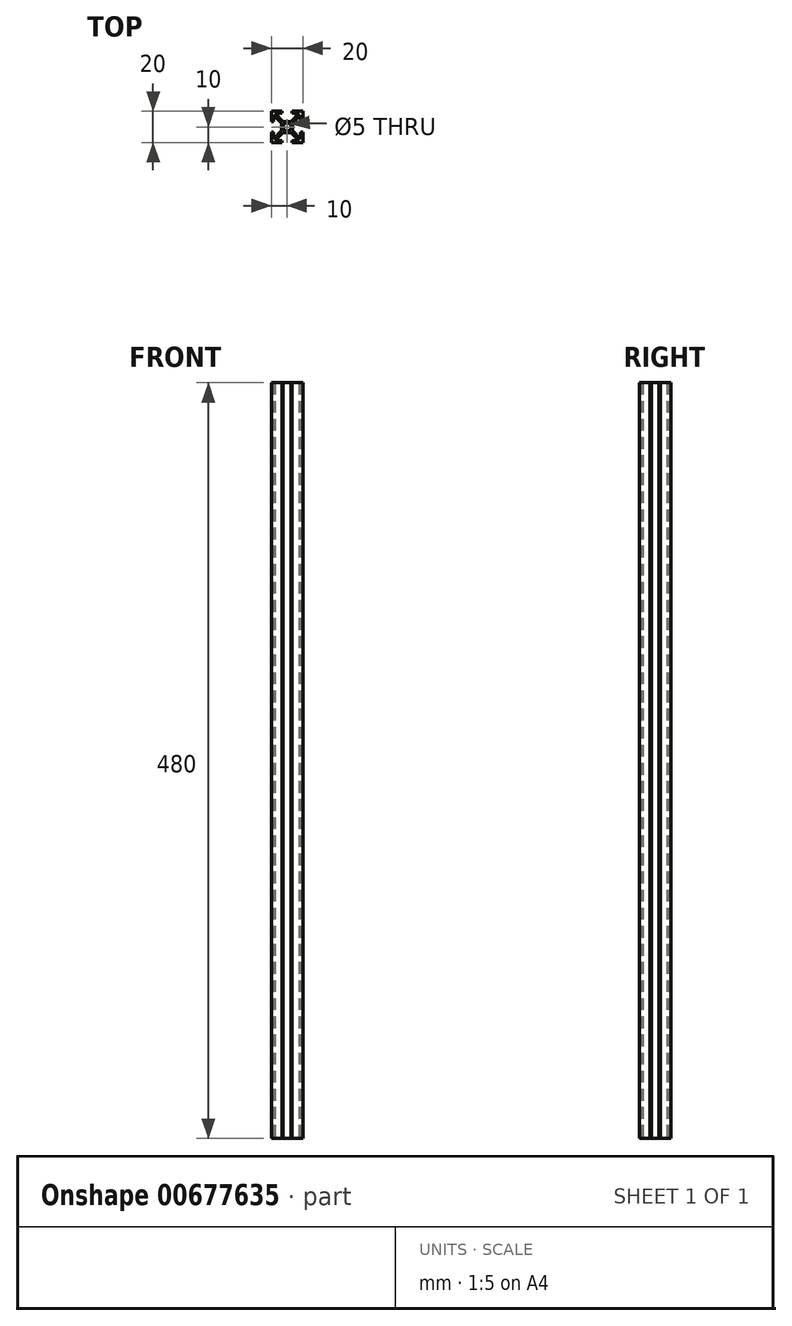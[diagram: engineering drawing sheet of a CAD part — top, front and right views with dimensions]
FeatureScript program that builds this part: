
annotation { "Feature Type Name" : "Feature", "Feature Type Description" : "" }
export const myFeature = defineFeature(function(context is Context, id is Id, definition is map)
    precondition{}
    {
        {
            var Q0;
            Q0=qCreatedBy(makeId("Top.planeOp"),FACE);
            var sketch = newSketch(context, id + "F0", { "sketchPlane" : qUnion([Q0])});
            skCircle(sketch, "E0", {"center": v(10, 10) * mm, "radius": 2.5 * mm});
            skLineSegment(sketch, "E1", {"start": v(0, 0) * mm, "end": v(10, 10) * mm, "construction": true});
            skLineSegment(sketch, "E2", {"start": v(1.4, 2.39) * mm, "end": v(1.4, 6.8) * mm});
            skLineSegment(sketch, "E3", {"start": v(1.4, 6.8) * mm, "end": v(0, 6.8) * mm});
            skLineSegment(sketch, "E4", {"start": v(0, 6.8) * mm, "end": v(0, 0) * mm});
            skLineSegment(sketch, "E5", {"start": v(7.49, 6.5) * mm, "end": v(2.39, 1.4) * mm});
            skLineSegment(sketch, "E6", {"start": v(2.39, 1.4) * mm, "end": v(6.8, 1.4) * mm});
            skLineSegment(sketch, "E7", {"start": v(6.8, 1.4) * mm, "end": v(6.8, 0) * mm});
            skLineSegment(sketch, "E8", {"start": v(6.8, 0) * mm, "end": v(0, 0) * mm});
            skLineSegment(sketch, "E9", {"start": v(10, 10) * mm, "end": v(20, 20) * mm, "construction": true});
            skLineSegment(sketch, "E10", {"start": v(10, 10) * mm, "end": v(0, 20) * mm, "construction": true});
            skLineSegment(sketch, "E11", {"start": v(10, 10) * mm, "end": v(20, 0) * mm, "construction": true});
            skLineSegment(sketch, "E12", {"start": v(1.4, 17.61) * mm, "end": v(6.5, 12.51) * mm});
            skLineSegment(sketch, "E13", {"start": v(1.4, 17.61) * mm, "end": v(1.4, 13.2) * mm});
            skLineSegment(sketch, "E14", {"start": v(1.4, 13.2) * mm, "end": v(0, 13.2) * mm});
            skLineSegment(sketch, "E15", {"start": v(0, 13.2) * mm, "end": v(0, 20) * mm});
            skLineSegment(sketch, "E16", {"start": v(7.49, 13.5) * mm, "end": v(2.39, 18.6) * mm});
            skLineSegment(sketch, "E17", {"start": v(2.39, 18.6) * mm, "end": v(6.8, 18.6) * mm});
            skLineSegment(sketch, "E18", {"start": v(6.8, 18.6) * mm, "end": v(6.8, 20) * mm});
            skLineSegment(sketch, "E19", {"start": v(6.8, 20) * mm, "end": v(0, 20) * mm});
            skLineSegment(sketch, "E20", {"start": v(12.51, 13.5) * mm, "end": v(17.61, 18.6) * mm});
            skLineSegment(sketch, "E21", {"start": v(17.61, 18.6) * mm, "end": v(13.2, 18.6) * mm});
            skLineSegment(sketch, "E22", {"start": v(13.2, 18.6) * mm, "end": v(13.2, 20) * mm});
            skLineSegment(sketch, "E23", {"start": v(13.2, 20) * mm, "end": v(20, 20) * mm});
            skLineSegment(sketch, "E24", {"start": v(13.5, 12.51) * mm, "end": v(18.6, 17.61) * mm});
            skLineSegment(sketch, "E25", {"start": v(18.6, 17.61) * mm, "end": v(18.6, 13.2) * mm});
            skLineSegment(sketch, "E26", {"start": v(18.6, 13.2) * mm, "end": v(20, 13.2) * mm});
            skLineSegment(sketch, "E27", {"start": v(20, 13.2) * mm, "end": v(20, 20) * mm});
            skLineSegment(sketch, "E28", {"start": v(18.6, 2.39) * mm, "end": v(18.6, 6.8) * mm});
            skLineSegment(sketch, "E29", {"start": v(18.6, 6.8) * mm, "end": v(20, 6.8) * mm});
            skLineSegment(sketch, "E30", {"start": v(20, 6.8) * mm, "end": v(20, 0) * mm});
            skLineSegment(sketch, "E31", {"start": v(12.51, 6.5) * mm, "end": v(17.61, 1.4) * mm});
            skLineSegment(sketch, "E32", {"start": v(17.61, 1.4) * mm, "end": v(13.2, 1.4) * mm});
            skLineSegment(sketch, "E33", {"start": v(13.2, 1.4) * mm, "end": v(13.2, 0) * mm});
            skLineSegment(sketch, "E34", {"start": v(13.2, 0) * mm, "end": v(20, 0) * mm});
            skLineSegment(sketch, "E35", {"start": v(12.51, 6.5) * mm, "end": v(7.49, 6.5) * mm});
            skLineSegment(sketch, "E36", {"start": v(7.49, 13.5) * mm, "end": v(12.51, 13.5) * mm});
            skLineSegment(sketch, "E37", {"start": v(10, 10) * mm, "end": v(10, 0) * mm, "construction": true});
            skLineSegment(sketch, "E38", {"start": v(10, 10) * mm, "end": v(18.77, 10) * mm, "construction": true});
            skLineSegment(sketch, "E39", {"start": v(10, 10) * mm, "end": v(10, 20.74) * mm, "construction": true});
            skLineSegment(sketch, "E40", {"start": v(10, 10) * mm, "end": v(0, 10) * mm, "construction": true});
            skLineSegment(sketch, "E41.bottom", {"start": v(0, 0) * mm, "end": v(20, 0) * mm, "construction": true});
            skLineSegment(sketch, "E41.top", {"start": v(0, 20) * mm, "end": v(20, 20) * mm, "construction": true});
            skLineSegment(sketch, "E41.left", {"start": v(0, 0) * mm, "end": v(0, 20) * mm, "construction": true});
            skLineSegment(sketch, "E41.right", {"start": v(20, 0) * mm, "end": v(20, 20) * mm, "construction": true});
            skLineSegment(sketch, "E42", {"start": v(18.6, 2.39) * mm, "end": v(13.5, 7.49) * mm});
            skLineSegment(sketch, "E43", {"start": v(13.5, 7.49) * mm, "end": v(13.5, 12.51) * mm});
            skLineSegment(sketch, "E44", {"start": v(1.4, 2.39) * mm, "end": v(6.5, 7.62) * mm});
            skLineSegment(sketch, "E45", {"start": v(6.5, 7.62) * mm, "end": v(6.5, 12.51) * mm});
            skSolve(sketch);
        }
        {
            var Q0;
            Q0=makeQuery(id+"F0.imprint","IMPRINT",FACE,{"disambiguationData":[TD([[makeQuery(id+"F0.imprint","IMPRINT",EDGE,{"derivedFrom":sQuery(id+"F0.wireOp",EDGE,"E0")}),-1.0]])]});
            extrude(context, id + "F1", {"entities" : qUnion([Q0]), "depth" : 480 * mm, "offsetDistance" : 25 * mm});
        }
    });
